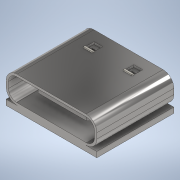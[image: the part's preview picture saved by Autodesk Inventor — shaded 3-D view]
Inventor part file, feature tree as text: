
AUTODESK INVENTOR PART (.ipt)
format: ipt  version: 2020 (Build 240168000, 168)  size: 314,368 bytes
history: native  units: in
note: dims shown in document units (in); Inventor stores cm internally (conversion verified against a paired STEP export)
features: extrude x7, sketch x4, chamfer x3
ambient origin geometry x8: Origin, YZ Plane, XZ Plane, XY Plane, X Axis, Y Axis, Z Axis, Center Point
bodies: Solid1 (feature_tree)
feature tree (14):
  extrude  "Extrusion1"  Depth=0.6593in
  sketch  "Sketch2"  dims[d2=0.2362in d3=0.0in d4=0.0394in]
  extrude  "Extrusion2"  Depth=0.0394in
  extrude  "Extrusion3"  Depth=0.0413in
  extrude  "Extrusion4"  Depth=0.0787in TaperAngle=0.0deg
  extrude  "Extrusion5"  Depth=0.5118in TaperAngle=0.0deg
  chamfer  "Chamfer1"  Distance=0.0787in
  chamfer  "Chamfer2"  Distance=0.0787in
  extrude  "Extrusion6"  Depth=0.0787in TaperAngle=45.0deg
  extrude  "Extrusion7"  Depth=0.0787in TaperAngle=45.0deg
  chamfer  "Chamfer3"  Distance=0.0551in
  sketch  "Sketch1"  dims[d0=0.5599in d1=0.6593in]
  sketch  "Sketch3"  dims[d6=0.0591in d7=4.7244in d9=0.0413in d10=0.3937in d12=0.3937in]
  sketch  "Sketch4"  dims[d14=0.0787in d15=0.5906in d16=0.0in d17=0.5118in d18=0.0in d19=0.0787in d20=0.0in d21=0.0787in d22=0.0in d23=0.0787in d24=0.0787in d25=45.0deg d26=0.0787in d27=0.0787in d28=45.0deg d29=0.0551in d30=0.063in d31=0.0276in d32=0.0in d33=0.0079in d34=0.0in d35=0.0098in d36=0.0787in d37=45.0deg]
